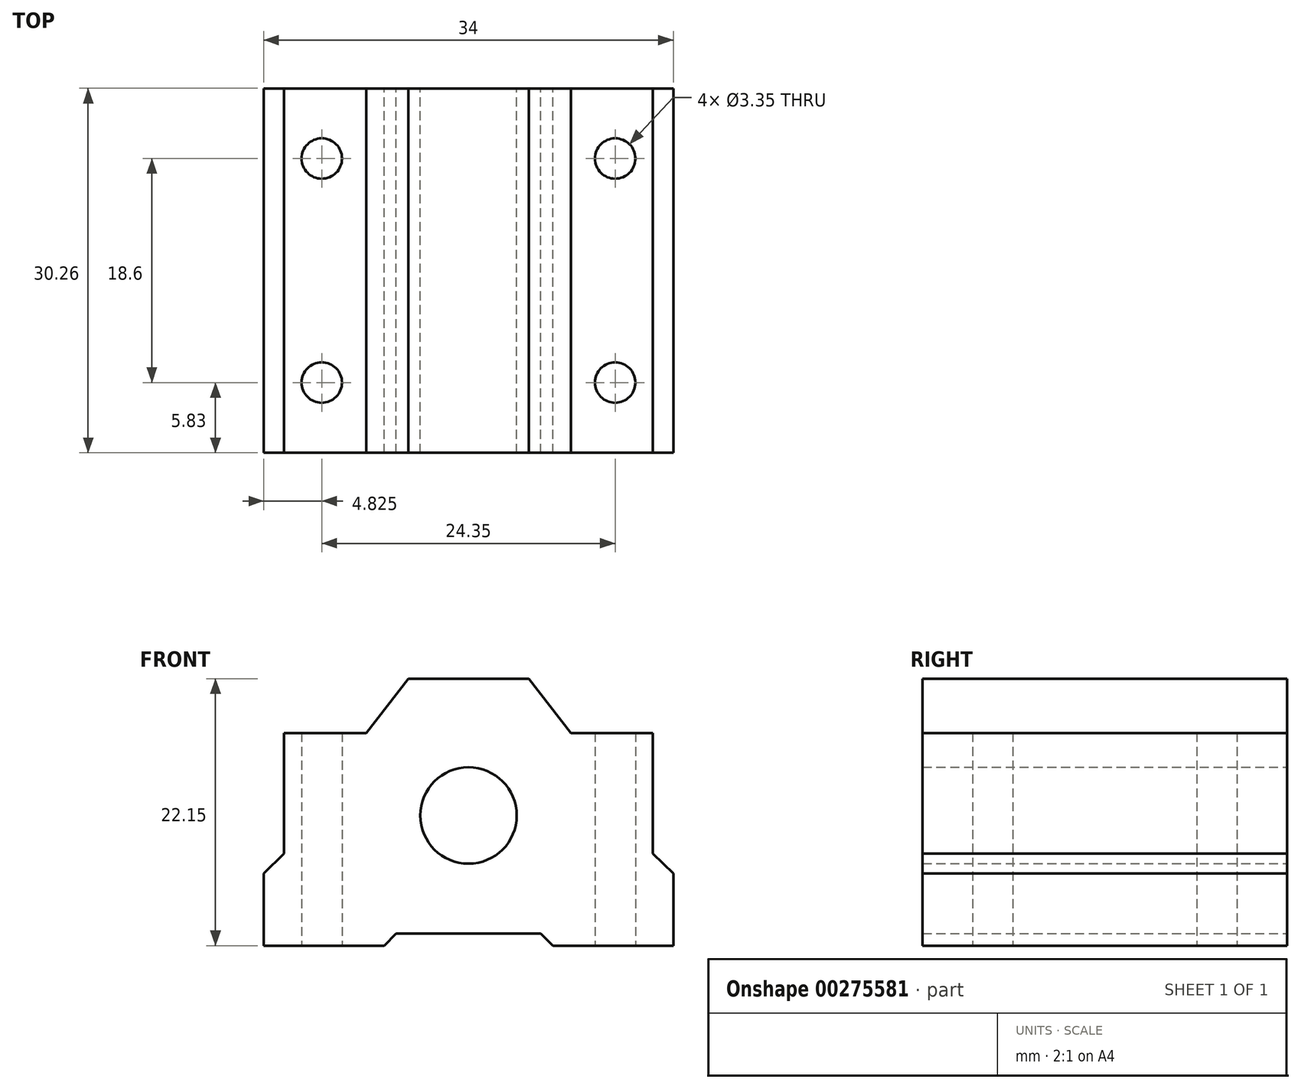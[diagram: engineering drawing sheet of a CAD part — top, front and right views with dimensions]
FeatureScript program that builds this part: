
annotation { "Feature Type Name" : "Feature", "Feature Type Description" : "" }
export const myFeature = defineFeature(function(context is Context, id is Id, definition is map)
    precondition{}
    {
        {
            var Q0;
            Q0=qCreatedBy(makeId("Front.planeOp"),FACE);
            var sketch = newSketch(context, id + "F0", { "sketchPlane" : qUnion([Q0])});
            skCircle(sketch, "E0", {"center": v(0, 0) * mm, "radius": 4 * mm});
            skLineSegment(sketch, "E1", {"start": v(0, 0) * mm, "end": v(0, 28.54) * mm, "construction": true});
            skLineSegment(sketch, "E2", {"start": v(-5, 11.35) * mm, "end": v(-8.5, 6.85) * mm});
            skLineSegment(sketch, "E3", {"start": v(-8.5, 6.85) * mm, "end": v(-15.3, 6.85) * mm});
            skLineSegment(sketch, "E4", {"start": v(-15.3, 6.85) * mm, "end": v(-15.3, -3.15) * mm});
            skLineSegment(sketch, "E5", {"start": v(-15.3, -3.15) * mm, "end": v(-17, -4.8) * mm});
            skLineSegment(sketch, "E6", {"start": v(-17, -4.8) * mm, "end": v(-17, -10.8) * mm});
            skLineSegment(sketch, "E7", {"start": v(-17, -10.8) * mm, "end": v(-7, -10.8) * mm});
            skLineSegment(sketch, "E8", {"start": v(-7, -10.8) * mm, "end": v(-6, -9.8) * mm});
            skLineSegment(sketch, "E9.MirrorCS", {"start": v(7, -10.8) * mm, "end": v(6, -9.8) * mm});
            skLineSegment(sketch, "E10.MirrorCS", {"start": v(17, -10.8) * mm, "end": v(7, -10.8) * mm});
            skLineSegment(sketch, "E11.MirrorCS", {"start": v(17, -4.8) * mm, "end": v(17, -10.8) * mm});
            skLineSegment(sketch, "E12.MirrorCS", {"start": v(15.3, -3.15) * mm, "end": v(17, -4.8) * mm});
            skLineSegment(sketch, "E13.MirrorCS", {"start": v(15.3, 6.85) * mm, "end": v(15.3, -3.15) * mm});
            skLineSegment(sketch, "E14.MirrorCS", {"start": v(8.5, 6.85) * mm, "end": v(15.3, 6.85) * mm});
            skLineSegment(sketch, "E15.MirrorCS", {"start": v(5, 11.35) * mm, "end": v(8.5, 6.85) * mm});
            skLineSegment(sketch, "E16", {"start": v(-5, 11.35) * mm, "end": v(5, 11.35) * mm});
            skLineSegment(sketch, "E17", {"start": v(-6, -9.8) * mm, "end": v(6, -9.8) * mm});
            skSolve(sketch);
        }
        {
            var Q0;
            Q0=qSketchRegion(id+"F0",true);
            extrude(context, id + "F1", {"entities" : qUnion([Q0]), "endBound" : BoundingType.SYMMETRIC, "depth" : 30.25 * mm});
        }
        {
            var Q0;
            Q0=makeQuery(id+"F1.opExtrude","SWEPT_FACE",FACE,{"disambiguationData":[OSD([sQuery(id+"F0.wireOp",EDGE,"E7")])]});
            var sketch = newSketch(context, id + "F2", { "sketchPlane" : qUnion([Q0])});
            skLineSegment(sketch, "E18", {"start": v(0, 0) * mm, "end": v(0, 27.72) * mm, "construction": true});
            skCircle(sketch, "E19", {"center": v(-12.18, 9.3) * mm, "radius": 1.67 * mm});
            skLineSegment(sketch, "E20", {"start": v(0, 0) * mm, "end": v(-30.82, 0) * mm, "construction": true});
            skCircle(sketch, "E21.MirrorC", {"center": v(12.18, 9.3) * mm, "radius": 1.67 * mm});
            skCircle(sketch, "E22.MirrorC", {"center": v(-12.18, -9.3) * mm, "radius": 1.67 * mm});
            skCircle(sketch, "E23.MirrorC", {"center": v(12.18, -9.3) * mm, "radius": 1.67 * mm});
            skSolve(sketch);
        }
        {
            var Q0;
            Q0=qSketchRegion(id+"F2",true);
            extrude(context, id + "F3", {"entities" : qUnion([Q0]), "operationType" : NewBodyOperationType.REMOVE, "endBound" : BoundingType.THROUGH_ALL, "oppositeDirection" : true, "depth" : 25 * mm});
        }
    });
